# Revit family: DSX_Unterputzschrank_3200-36039
name_source: partatom
category: HLS-Bauteile
units: mm (PartAtom-declared; Revit-internal decimal feet)

## family parameters
Arbeitsebenenbasiert = Nein
Beim Laden mit Abzugskörper schneiden = Nein
Bemaßung runder Anschluss = Durchmesser verwenden
Beschriftungsausrichtung beibehalten = Nein
Gemeinsam genutzt = Nein
Immer vertikal = Ja
Klassifizierung = Keine
OmniClass-Nummer = 23.65.35.11.14
OmniClass-Titel = Instantaneous Water Heaters
Raumberechnungspunkt = Nein
Teiletyp = Normal

## types (1)
- Unterputzschrank mit einzelnem DSX
    Art_Nr1 = 3200
    Art_Nr2 = 36039
    Beschreibung = DSX Unterputzschrank mit Gerät
    Hersteller = CLAGE GmbH
    Kaltwasseranschluss_Durchmesser = 21 mm  [stored 0.0688976 ft]
    Materialstärke = 1 mm  [stored 0.00328084 ft]
    Modell = 3200-36039
    Vorgabe-Ansicht = 0 mm  [stored 0 ft]
    Warmwasseranschluss_Durchmesser = 21 mm  [stored 0.0688976 ft]

note: [stored X ft] marks values corroborated as IEEE doubles in the binary element streams (Revit-internal decimal feet)
